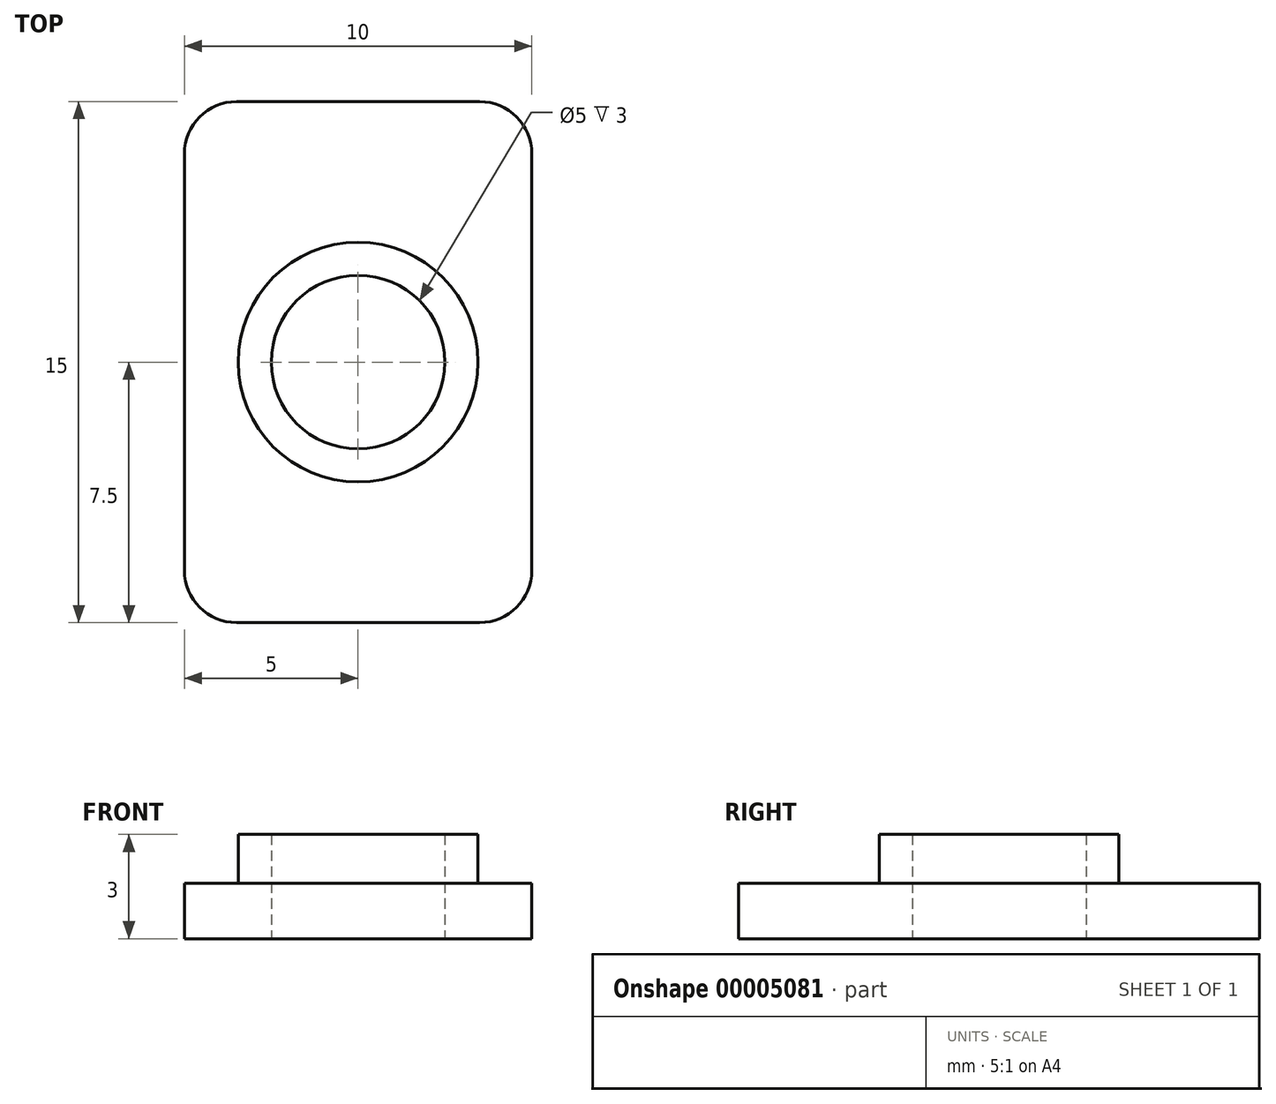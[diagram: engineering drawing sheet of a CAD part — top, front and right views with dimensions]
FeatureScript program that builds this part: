
annotation { "Feature Type Name" : "Feature", "Feature Type Description" : "" }
export const myFeature = defineFeature(function(context is Context, id is Id, definition is map)
    precondition{}
    {
        {
            var Q0;
            Q0=qCreatedBy(makeId("Top.planeOp"),FACE);
            var sketch = newSketch(context, id + "F0", { "sketchPlane" : qUnion([Q0])});
            skLineSegment(sketch, "E0.rect.bottom", {"start": v(3.5, 7.5) * mm, "end": v(-3.5, 7.5) * mm});
            skLineSegment(sketch, "E0.rect.top", {"start": v(3.5, -7.5) * mm, "end": v(-3.5, -7.5) * mm});
            skLineSegment(sketch, "E0.rect.left", {"start": v(5, 6) * mm, "end": v(5, -6) * mm});
            skLineSegment(sketch, "E0.rect.right", {"start": v(-5, 6) * mm, "end": v(-5, -6) * mm});
            skPoint(sketch, "E0.rect.middle", {"position": v(0, 0) * mm});
            skPoint(sketch, "E1.visualSharp", {"position": v(-5, 7.5) * mm});
            skArc(sketch, "E1.filletArc", {"start": v(-3.5, 7.5) * mm, "mid": v(-4.56, 7.06) * mm, "end": v(-5, 6) * mm});
            skPoint(sketch, "E2.visualSharp", {"position": v(-5, -7.5) * mm});
            skArc(sketch, "E2.filletArc", {"start": v(-5, -6) * mm, "mid": v(-4.56, -7.06) * mm, "end": v(-3.5, -7.5) * mm});
            skPoint(sketch, "E3.visualSharp", {"position": v(5, -7.5) * mm});
            skArc(sketch, "E3.filletArc", {"start": v(3.5, -7.5) * mm, "mid": v(4.56, -7.06) * mm, "end": v(5, -6) * mm});
            skPoint(sketch, "E4.visualSharp", {"position": v(5, 7.5) * mm});
            skArc(sketch, "E4.filletArc", {"start": v(5, 6) * mm, "mid": v(4.56, 7.06) * mm, "end": v(3.5, 7.5) * mm});
            skCircle(sketch, "E5", {"center": v(0, 0) * mm, "radius": 2.5 * mm});
            skSolve(sketch);
        }
        {
            var Q0;
            Q0=makeQuery(id+"F0.imprint","IMPRINT",FACE,{"disambiguationData":[TD([[makeQuery(id+"F0.imprint","IMPRINT",EDGE,{"derivedFrom":sQuery(id+"F0.wireOp",EDGE,"E0.rect.bottom")}),1.0]])]});
            extrude(context, id + "F1", {"entities" : qUnion([Q0]), "depth" : 1.6 * mm});
        }
        {
            var Q0;
            Q0=makeQuery(id+"F1.opExtrude","CAP_FACE",FACE,{"disambiguationData":[OSD([sQuery(id+"F0.wireOp",EDGE,"E0.rect.bottom"),sQuery(id+"F0.wireOp",EDGE,"E0.rect.top"),sQuery(id+"F0.wireOp",EDGE,"E0.rect.left"),sQuery(id+"F0.wireOp",EDGE,"E0.rect.right"),sQuery(id+"F0.wireOp",EDGE,"E1.filletArc"),sQuery(id+"F0.wireOp",EDGE,"E2.filletArc"),sQuery(id+"F0.wireOp",EDGE,"E3.filletArc"),sQuery(id+"F0.wireOp",EDGE,"E4.filletArc"),sQuery(id+"F0.wireOp",EDGE,"E5")])],"isStart":false});
            var sketch = newSketch(context, id + "F2", { "sketchPlane" : qUnion([Q0])});
            skCircle(sketch, "E6", {"center": v(0, 0) * mm, "radius": 2.5 * mm});
            skCircle(sketch, "E7", {"center": v(0, 0) * mm, "radius": 3.45 * mm});
            skSolve(sketch);
        }
        {
            var Q0;
            Q0=makeQuery(id+"F2.imprint","IMPRINT",FACE,{"disambiguationData":[TD([[makeQuery(id+"F2.imprint","IMPRINT",EDGE,{"derivedFrom":sQuery(id+"F2.wireOp",EDGE,"E6")}),-1.0]])]});
            extrude(context, id + "F3", {"entities" : qUnion([Q0]), "operationType" : NewBodyOperationType.ADD, "depth" : 1.4 * mm});
        }
    });
